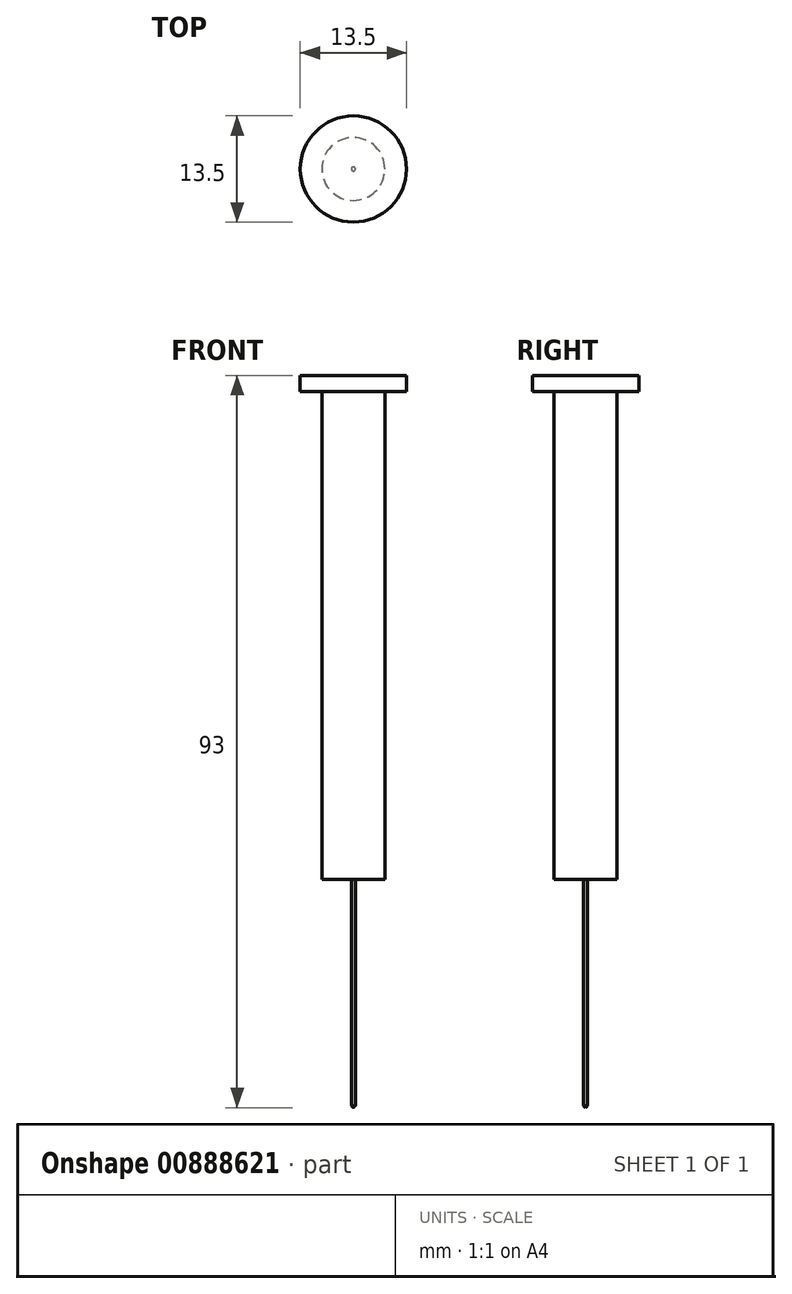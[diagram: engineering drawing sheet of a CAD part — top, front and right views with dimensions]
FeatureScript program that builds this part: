
annotation { "Feature Type Name" : "Feature", "Feature Type Description" : "" }
export const myFeature = defineFeature(function(context is Context, id is Id, definition is map)
    precondition{}
    {
        {
            var Q0;
            Q0=qCreatedBy(makeId("Top.planeOp"),FACE);
            var sketch = newSketch(context, id + "F0", { "sketchPlane" : qUnion([Q0])});
            skCircle(sketch, "E0", {"center": v(0, 0) * mm, "radius": 6.75 * mm});
            skSolve(sketch);
        }
        {
            var Q0;
            Q0=makeQuery(id+"F0.imprint","IMPRINT",FACE,{"disambiguationData":[TD([[makeQuery(id+"F0.imprint","IMPRINT",EDGE,{"derivedFrom":sQuery(id+"F0.wireOp",EDGE,"E0")}),1.0]])]});
            extrude(context, id + "F1", {"entities" : qUnion([Q0]), "depth" : 2 * mm, "offsetDistance" : 25 * mm});
        }
        {
            var Q0;
            Q0=makeQuery(id+"F1.opExtrude","CAP_FACE",FACE,{"disambiguationData":[OSD([sQuery(id+"F0.wireOp",EDGE,"E0")])],"isStart":true});
            var sketch = newSketch(context, id + "F2", { "sketchPlane" : qUnion([Q0])});
            skCircle(sketch, "E1", {"center": v(0, 0) * mm, "radius": 4 * mm});
            skSolve(sketch);
        }
        {
            var Q0;
            Q0=makeQuery(id+"F2.imprint","IMPRINT",FACE,{"disambiguationData":[TD([[makeQuery(id+"F2.imprint","IMPRINT",EDGE,{"derivedFrom":sQuery(id+"F2.wireOp",EDGE,"E1")}),1.0]])]});
            extrude(context, id + "F3", {"entities" : qUnion([Q0]), "operationType" : NewBodyOperationType.ADD, "depth" : 62 * mm, "offsetDistance" : 25 * mm});
        }
        {
            var Q0;
            Q0=makeQuery(id+"F3.opExtrude","CAP_FACE",FACE,{"disambiguationData":[OSD([sQuery(id+"F2.wireOp",EDGE,"E1")])],"isStart":false});
            var sketch = newSketch(context, id + "F4", { "sketchPlane" : qUnion([Q0])});
            skCircle(sketch, "E2", {"center": v(0, 0) * mm, "radius": 0.25 * mm});
            skSolve(sketch);
        }
        {
            var Q0;
            Q0=makeQuery(id+"F4.imprint","IMPRINT",FACE,{"disambiguationData":[TD([[makeQuery(id+"F4.imprint","IMPRINT",EDGE,{"derivedFrom":sQuery(id+"F4.wireOp",EDGE,"E2")}),1.0]])]});
            extrude(context, id + "F5", {"entities" : qUnion([Q0]), "operationType" : NewBodyOperationType.ADD, "depth" : 29 * mm, "offsetDistance" : 25 * mm});
        }
        {
            var Q0;
            Q0=makeQuery(id+"F5.opExtrude","CAP_FACE",FACE,{"disambiguationData":[OSD([sQuery(id+"F4.wireOp",EDGE,"E2")])],"isStart":false});
            chamfer(context, id + "F6", {"entities" : qUnion([Q0]), "width" : 0.25 * mm, "tangentPropagation" : true});
        }
    });
